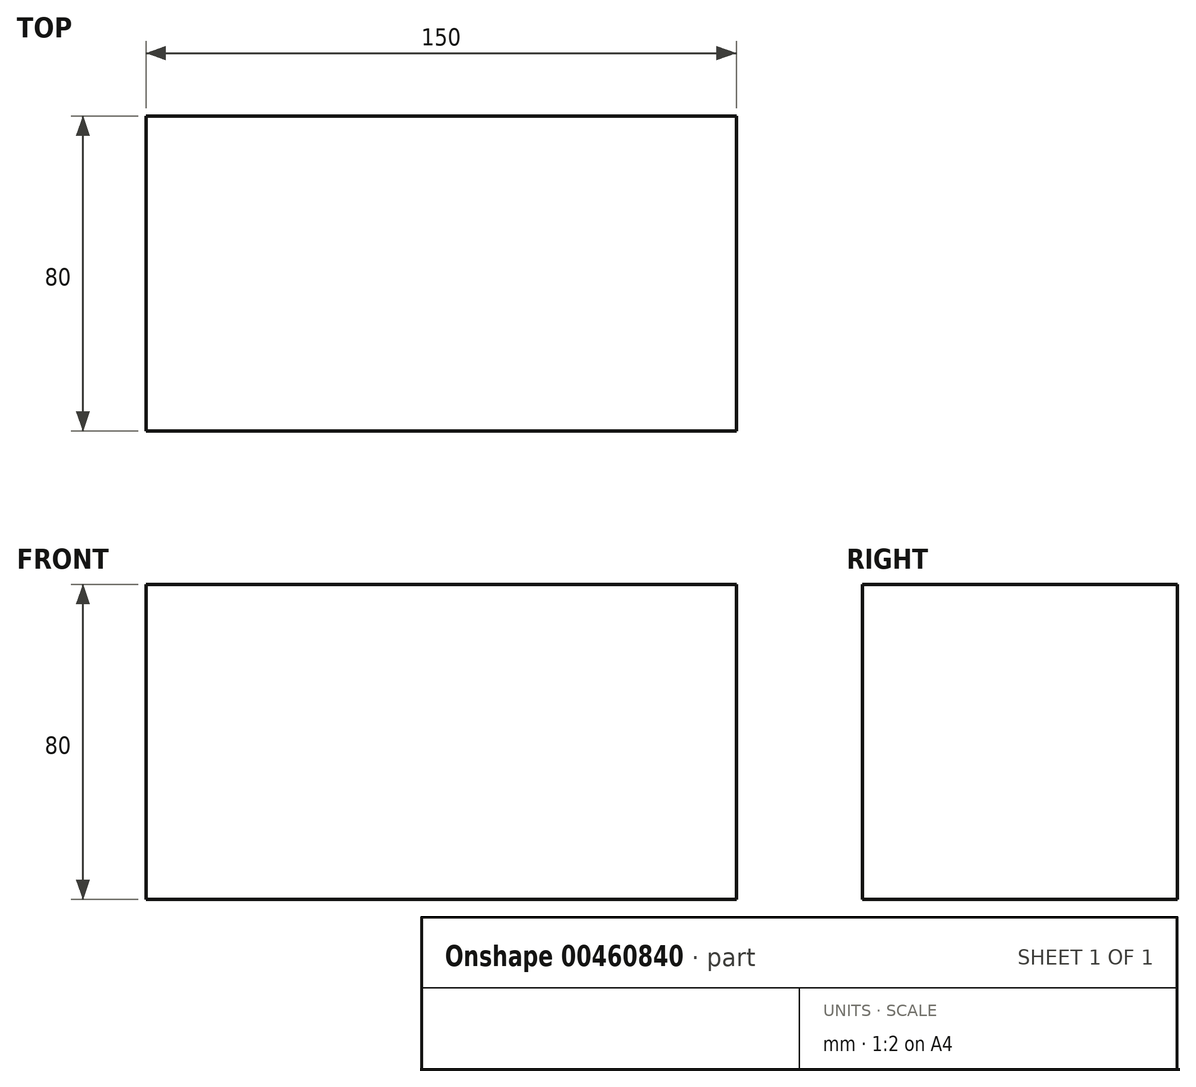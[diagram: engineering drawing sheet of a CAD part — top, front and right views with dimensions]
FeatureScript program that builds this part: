
annotation { "Feature Type Name" : "Feature", "Feature Type Description" : "" }
export const myFeature = defineFeature(function(context is Context, id is Id, definition is map)
    precondition{}
    {
        {
            var Q0;
            Q0=qCreatedBy(makeId("Top.planeOp"),FACE);
            var sketch = newSketch(context, id + "F0", { "sketchPlane" : qUnion([Q0])});
            skLineSegment(sketch, "E0.bottom", {"start": v(75, -40) * mm, "end": v(-75, -40) * mm});
            skLineSegment(sketch, "E0.top", {"start": v(75, 40) * mm, "end": v(-75, 40) * mm});
            skLineSegment(sketch, "E0.left", {"start": v(75, -40) * mm, "end": v(75, 40) * mm});
            skLineSegment(sketch, "E0.right", {"start": v(-75, -40) * mm, "end": v(-75, 40) * mm});
            skPoint(sketch, "E0.middle", {"position": v(0, 0) * mm});
            skSolve(sketch);
        }
        {
            var Q0;
            Q0 = qSketchRegion(id + "F0", true);
            extrude(context, id + "F1", {"entities" : qUnion([Q0]), "depth" : 80 * mm});
        }
    });
